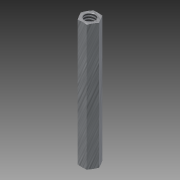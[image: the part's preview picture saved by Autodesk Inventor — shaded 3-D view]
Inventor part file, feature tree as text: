
AUTODESK INVENTOR PART (.ipt)
format: ipt  version: 2011 (Build 150239000, 239)  size: 116,224 bytes
history: native  units: in
note: dims shown in document units (in); Inventor stores cm internally (conversion verified against a paired STEP export)
features: thread x2, other x1, imported_body x1
ambient origin geometry x8: Origin, YZ Plane, XZ Plane, XY Plane, X Axis, Y Axis, Z Axis, Center Point
feature tree (4):
  parser-record x1  (decoder bookkeeping rows leaked as tree rows — omitted from the tree; the rows remain in map.json)
  imported_body  "Base1"
  thread  "Thread1"  [1 undecoded]
  thread  "Thread2"  [1 undecoded]
note: 2 required parameter values undecoded (feature->parameter linkage not recoverable at this tier; creation-order binding heuristic only, values carry confidence <= 0.55)
